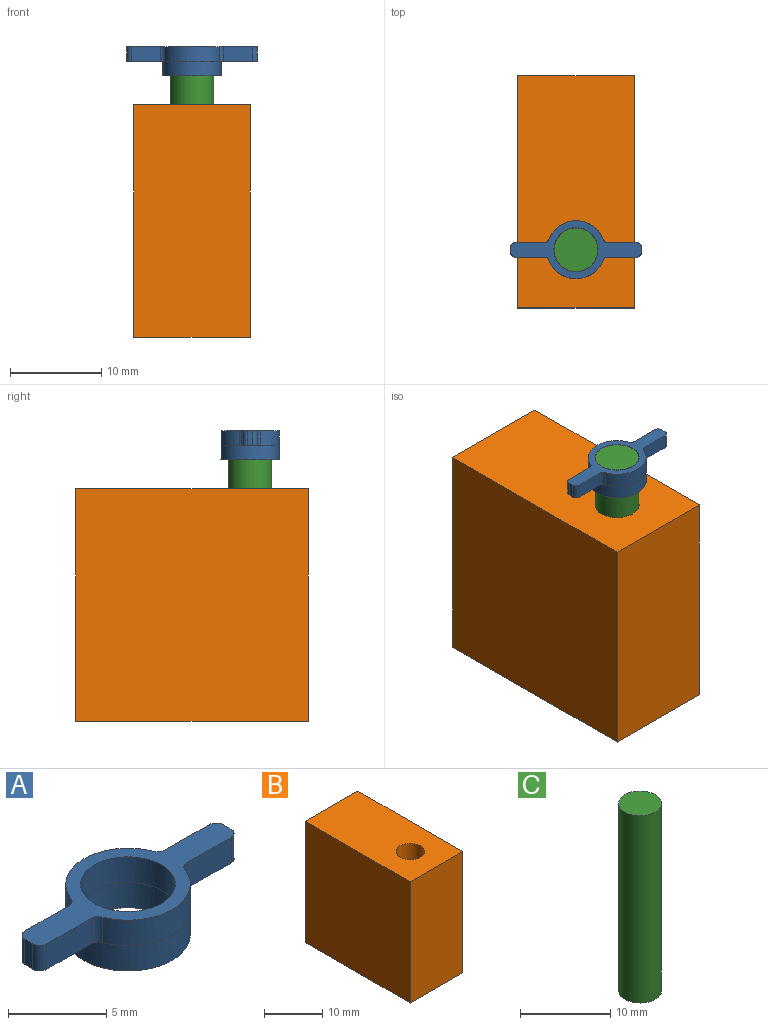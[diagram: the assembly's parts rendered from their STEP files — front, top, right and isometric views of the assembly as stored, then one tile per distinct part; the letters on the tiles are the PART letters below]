
ASSEMBLY  parts=3 mates=1
PART A: 23 faces, bbox 14.3x6.4x3.2 mm
  f0: plane 4.18x2.25mm, normal (0,0,-1), area 6.3mm2, adj f5,f6,f7,f13,f18,f19,f20,f21
  f1: plane 3.19x1.59mm, normal (0,1,0), area 5.1mm2, adj f10,f11,f15,f22
  f2: plane 1.59x0.57mm, normal (-1,0,0), area 0.9mm2, adj f10,f11,f15,f16
  f3: plane 3.19x1.59mm, normal (0,-1,0), area 5.1mm2, adj f10,f11,f16,f17
  f4: cylinder r=3.17mm len=5.94mm, axis (0,0,1), area 12.2mm2, adj f11,f13,f17,f18
  f5: plane 3.19x1.59mm, normal (0,-1,0), area 5.1mm2, adj f0,f11,f18,f19
  f6: plane 1.59x0.57mm, normal (1,0,0), area 0.9mm2, adj f0,f11,f19,f20
  f7: plane 3.19x1.59mm, normal (0,1,0), area 5.1mm2, adj f0,f11,f20,f21
  f8: cylinder r=3.17mm len=5.94mm, axis (0,0,1), area 12.2mm2, adj f11,f13,f21,f22
  f9: cylinder r=2.41mm len=4.83mm, axis (0,0,1), area 24.1mm2, adj f11,f14
  f10: plane 4.18x2.22mm, normal (0,0,-1), area 6.3mm2, adj f1,f2,f3,f13,f15,f16,f17,f22
  f11: plane 14.29x6.35mm, normal (0,0,1), area 26mm2, adj f1,f2,f3,f4,f5,f6,f7,f8
  f12: plane 6.35x6.35mm, normal (0,0,-1), area 13.4mm2, adj f13,f14
  f13: cylinder r=3.17mm len=6.35mm, axis (0,0,1), area 31.7mm2, adj f0,f4,f8,f10,f12,f22
  f14: cylinder r=2.41mm len=4.83mm, axis (0,0,-1), area 24.1mm2, adj f9,f12
  f15: cylinder r=0.51mm len=1.59mm, axis (0,0,1), area 1.3mm2, adj f1,f2,f10,f11
  f16: cylinder r=0.51mm len=1.59mm, axis (0,0,-1), area 1.3mm2, adj f2,f3,f10,f11
  f17: cylinder r=0.51mm len=1.59mm, axis (0,0,1), area 1mm2, adj f3,f4,f10,f11
  f18: cylinder r=0.51mm len=1.59mm, axis (0,0,1), area 1mm2, adj f0,f4,f5,f11
  f19: cylinder r=0.51mm len=1.59mm, axis (0,0,-1), area 1.3mm2, adj f0,f5,f6,f11
  f20: cylinder r=0.51mm len=1.59mm, axis (0,0,1), area 1.3mm2, adj f0,f6,f7,f11
  f21: cylinder r=0.51mm len=1.59mm, axis (0,0,1), area 1mm2, adj f0,f7,f8,f11
  f22: cylinder r=0.51mm len=1.59mm, axis (0,0,1), area 1mm2, adj f1,f8,f10,f11,f13
PART B: 8 faces, bbox 12.7x25.4x25.4 mm
  f0: plane 25.4x12.7mm, normal (0,-1,0), area 322.6mm2, adj f1,f3,f4,f5
  f1: plane 25.4x25.4mm, normal (1,0,0), area 645.2mm2, adj f0,f2,f4,f5
  f2: plane 25.4x12.7mm, normal (0,1,0), area 322.6mm2, adj f1,f3,f4,f5
  f3: plane 25.4x25.4mm, normal (-1,0,0), area 645.2mm2, adj f0,f2,f4,f5
  f4: plane 25.4x12.7mm, normal (0,0,1), area 304.3mm2, adj f0,f1,f2,f3,f6
  f5: plane 25.4x12.7mm, normal (0,0,-1), area 322.6mm2, adj f0,f1,f2,f3
  f6: cylinder r=2.41mm len=19.05mm, axis (0,0,1), area 288.8mm2, adj f4,f7
  f7: plane 4.83x4.83mm, normal (0,0,1), area 18.3mm2, adj f6
PART C: 3 faces, bbox 4.8x4.8x25.4 mm
  f0: cylinder r=2.38mm len=25.4mm, axis (0,0,-1), area 380mm2, adj f1,f2
  f1: plane 4.76x4.76mm, normal (0,0,1), area 17.8mm2, adj f0
  f2: plane 4.76x4.76mm, normal (0,0,-1), area 17.8mm2, adj f0
PLACE A t=(0,-57.46,0)mm
PLACE B at identity fixed
PLACE C t=(0,-32.93,0)mm
MATE fastened C.f0 <-> A.f9  axis (0,0,1) through (0,-6.35,31.75)mm
